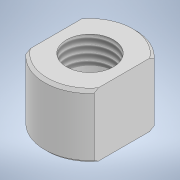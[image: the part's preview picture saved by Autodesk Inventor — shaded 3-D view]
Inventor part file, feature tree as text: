
AUTODESK INVENTOR PART (.ipt)
format: ipt  version: 2021 (Build 250183000, 183)  size: 131,072 bytes
history: native  units: mm
features: sketch x4, extrude x2, hole x2, chamfer x1
ambient origin geometry x8: Origin, YZ Plane, XZ Plane, XY Plane, X Axis, Y Axis, Z Axis, Center Point
bodies: Solid1 (feature_tree)
feature tree (9):
  extrude  "Extrusion1"  Depth=14.0mm TaperAngle=0.0deg
  hole  "Hole1"  [1 undecoded]
  hole  "Hole2"  [1 undecoded]
  chamfer  "Chamfer1"  [1 undecoded]
  extrude  "Extrusion2"  [1 undecoded]
  sketch  "Sketch1"  dims[d0=20.0mm d1=14.0mm d2=0.0mm]
  sketch  "Sketch2"  dims[d3=10.376mm d4=6.0mm d5=4.0mm d6=2.0mm d7=90.0deg d8=9.0mm d9=20.594885mm]
  sketch  "Sketch3"  dims[d10=3.9624mm d11=9.652mm d12=4.0mm d13=2.0mm d14=90.0deg d15=13.621mm d16=20.594885mm d17=0.6mm d18=2.0mm d19=45.0deg]
  sketch  "Sketch4"  dims[d20=15.0mm d21=14.0mm d22=0.0mm]
note: 4 required parameter values undecoded (feature->parameter linkage not recoverable at this tier; creation-order binding heuristic only, values carry confidence <= 0.55)
